# Revit family: EKF_EE_БоковыеПанелиTrivia_AVERES
name_source: partatom
category: Электрооборудование
units: mm (PartAtom-declared; Revit-internal decimal feet)

## family parameters
Всегда вертикально = Нет
На основе рабочей плоскости = Да
Общий = Да
При загрузке вырезать с полостями = Нет
Размер круглого соединителя = Использовать диаметр
Тип детали = Силовой щит
Точка расчета площади = Нет

## types (6) — shared parameters
ADSK_Единица измерения = шт.
ADSK_Завод-изготовитель = EKF
ADSK_Количество = 1
ADSK_Марка = Боковые панели
ADSK_Материал = RAL 7035_Сталь
ADSK_Обозначение = Боковые панели
ADSK_Размер_Высота = 2007 мм
ADSK_Размер_Глубина = 14 мм
Изготовитель = EKF
Отметка по умолчанию = 1219.2 мм
Серия номенклатуры = Averes
ТВ = EKF_2_TRIVIA_AVERES
Тип установки = -
zero-valued in all types: ADSK_Масса

## per-type parameters (varying)
| type | ADSK_Код изделия | ADSK_Наименование | ADSK_Размер_Ширина | Степень защиты IP | Тип |
| Боковые панели Г400 IP30 (2 шт) EKF AVERES | PS400 | Боковые панели Г400 IP30 (2 шт) EKF AVERES | 410 мм | IP30 | 419 мм |
| Боковые панели Г400 IP55 (2 шт) EKF AVERES | PS400WP | Боковые панели Г400 IP55 (2 шт) EKF AVERES | 410 мм | IP55 | 420 мм |
| Боковые панели Г600 IP30 (2 шт) EKF AVERES | PS600 | Боковые панели Г600 IP30 (2 шт) EKF AVERES | 610 мм | IP30 | 421 мм |
| Боковые панели Г600 IP55 (2 шт)  EKF AVERES | PS600WP | Боковые панели Г600 IP55 (2 шт) EKF AVERES | 610 мм | IP55 | 422 мм |
| Боковые панели Г800 IP30 (2 шт) EKF AVERES | PS800 | Боковые панели Г800 IP30 (2 шт) EKF AVERES | 810 мм | IP30 | 423 мм |
| Боковые панели Г800 IP55 (2 шт) EKF AVERES | PS800WP | Боковые панели Г800 IP55 (2 шт) EKF AVERES | 810 мм | IP55 | 424 мм |
